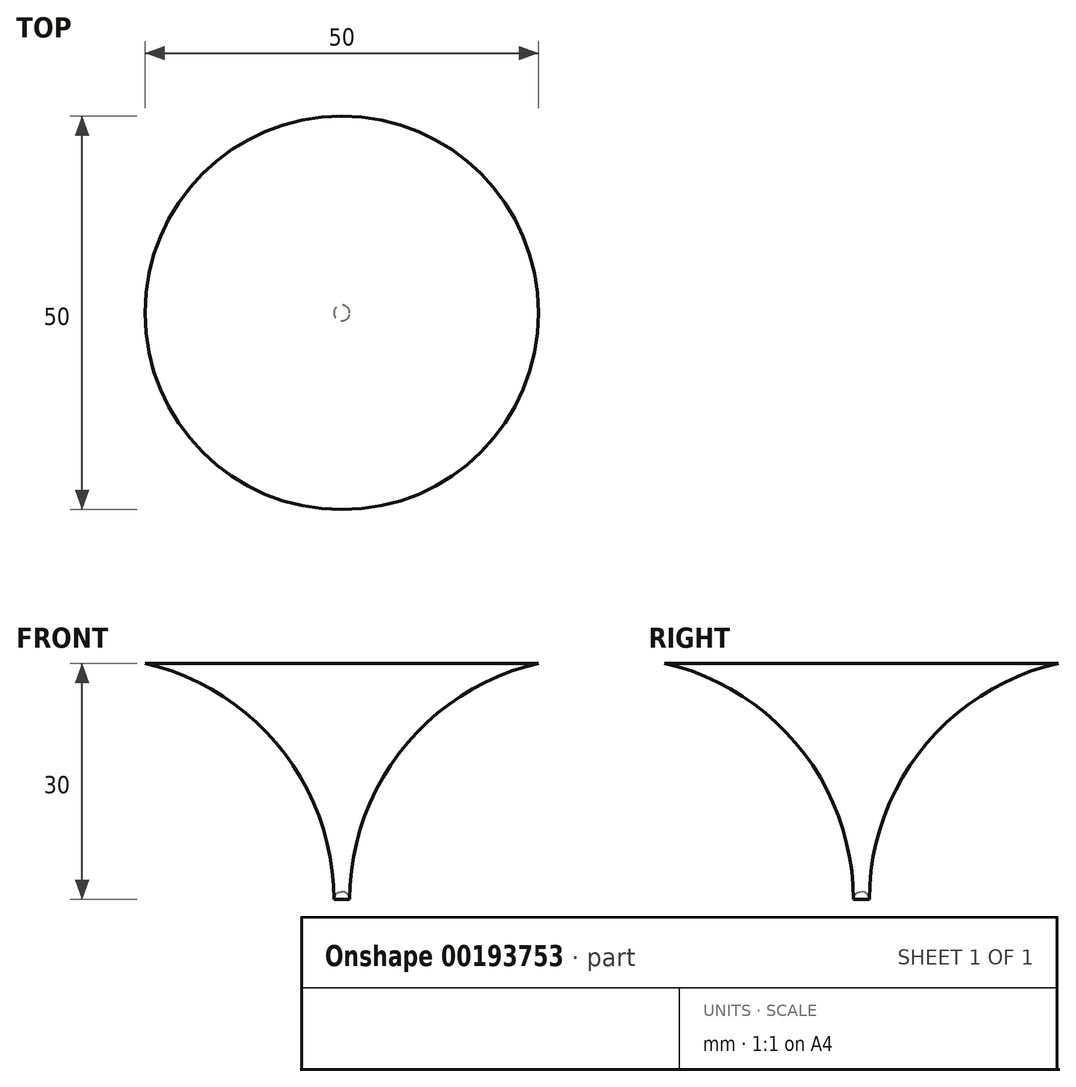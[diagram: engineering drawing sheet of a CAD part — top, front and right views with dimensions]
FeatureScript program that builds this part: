
annotation { "Feature Type Name" : "Feature", "Feature Type Description" : "" }
export const myFeature = defineFeature(function(context is Context, id is Id, definition is map)
    precondition{}
    {
        {
            var Q0;
            Q0=qCreatedBy(makeId("Front.planeOp"),FACE);
            var sketch = newSketch(context, id + "F0", { "sketchPlane" : qUnion([Q0])});
            skLineSegment(sketch, "E0", {"start": v(-25, 30) * mm, "end": v(0, 30) * mm});
            skLineSegment(sketch, "E1", {"start": v(0, 30) * mm, "end": v(0, 0) * mm});
            skArc(sketch, "E2", {"start": v(-1, 0) * mm, "mid": v(-7.78, 19.18) * mm, "end": v(-25, 30) * mm});
            skLineSegment(sketch, "E3", {"start": v(0, 0) * mm, "end": v(-1, 0) * mm});
            skArc(sketch, "E4", {"start": v(-1, 0) * mm, "mid": v(-0.7, -0.7) * mm, "end": v(0, -1) * mm});
            skLineSegment(sketch, "E5", {"start": v(0, 0) * mm, "end": v(0, -1) * mm});
            skSolve(sketch);
        }
        {
            var Q0;
            Q0=makeQuery(id+"F0.imprint","IMPRINT",FACE,{"disambiguationData":[TD([[makeQuery(id+"F0.imprint","IMPRINT",EDGE,{"derivedFrom":sQuery(id+"F0.wireOp",EDGE,"E0")}),-1.0]])]});
            var Q1;
            Q1=makeQuery(id+"F0.imprint","IMPRINT",FACE,{"disambiguationData":[TD([[makeQuery(id+"F0.imprint","IMPRINT",EDGE,{"derivedFrom":sQuery(id+"F0.wireOp",EDGE,"E3")}),1.0]])]});
            var Q2;
            Q2=sQuery(id+"F0.wireOp",EDGE,"E1");
            revolve(context, id + "F1", {"entities" : qUnion([Q0, Q1]), "axis" : qUnion([Q2]), "revolveType" : RevolveType.FULL});
        }
    });
